# Revit family: Staberder_für_Standardanwendungen
name_source: partatom
category: Generic Models
revit_build: Autodesk Revit 2015 (Build: 20140606_1530(x64)
units: mm (PartAtom-declared; Revit-internal decimal feet)

## types (3) — shared parameters
Manufacturer = OBO Bettermann
Material = Steel, Galvanized
URL = http://www.obo-bettermann.com

## per-type parameters (varying)
| type | Article Type | Diameter dimesion | GTIN | Manufacturer Art. No. | Outer Diameter Dimension |
| 219 25 ST FT | 219 25 ST FT | 13 mm | 4012195111047 | 5000769 | 8 mm  [stored 0.0262467 ft] |
| 219 20 ST FT 1500 | 219 20 ST FT | 10 mm  [stored 0.0328084 ft] | 4012195814450 | 50000750 | 6 mm  [stored 0.019685 ft] |
| 219 20 ST FT 1000 | 219 20 ST FT | 10 mm  [stored 0.0328084 ft] | 4012195018049 | 50000742 | 6 mm  [stored 0.019685 ft] |

note: [stored X ft] marks values corroborated as IEEE doubles in the binary element streams (Revit-internal decimal feet)

## geometry (parser evidence)
native form markers: Sweep x2
no freeform markers — native parametric forms only
